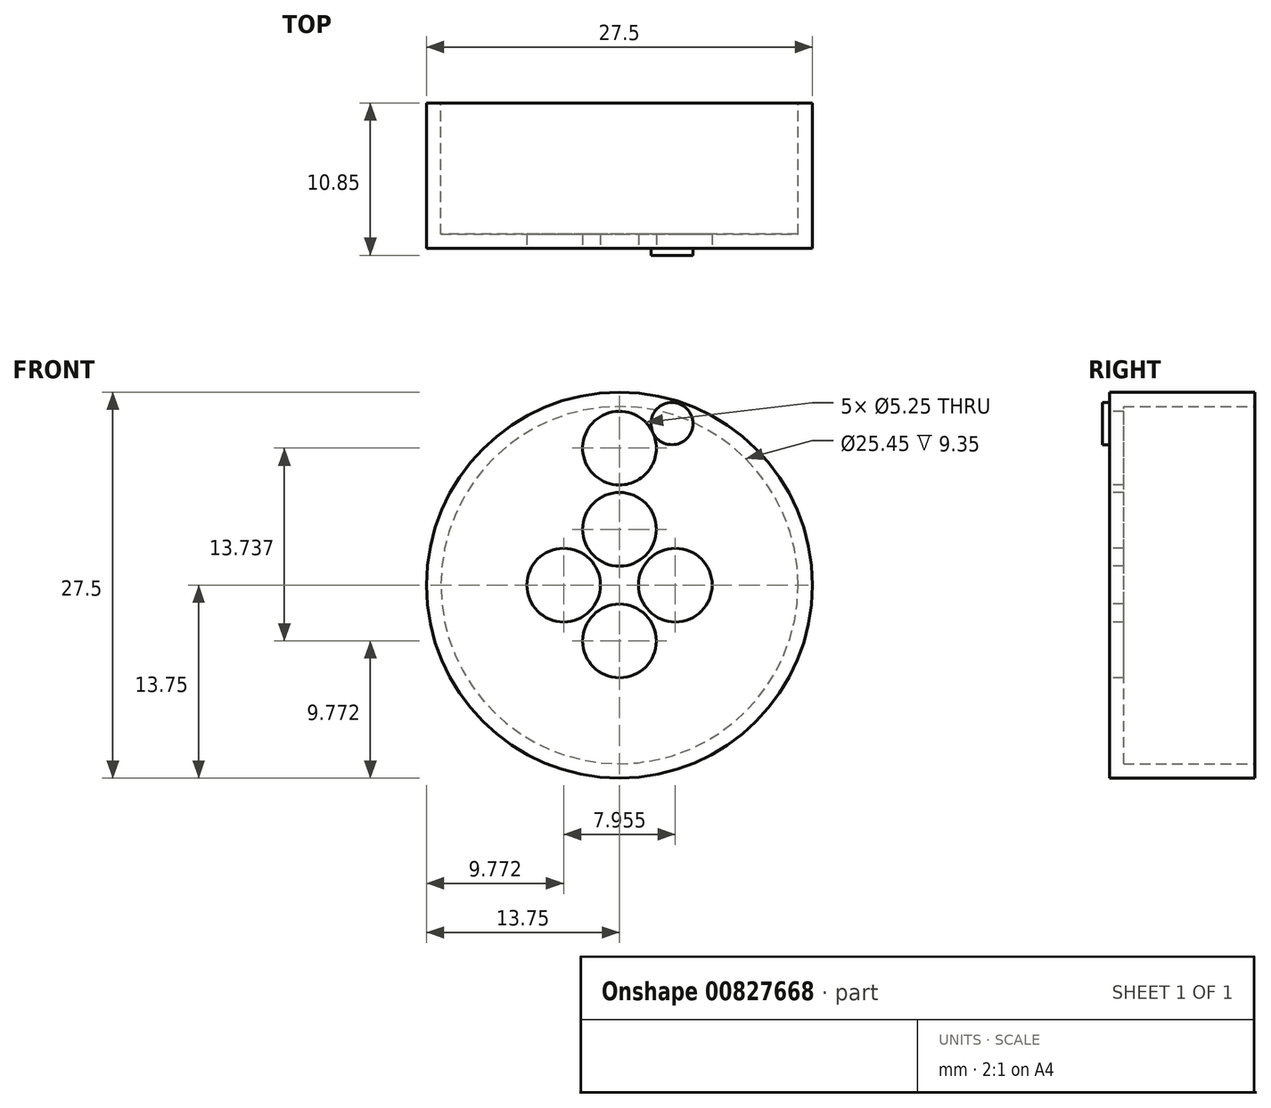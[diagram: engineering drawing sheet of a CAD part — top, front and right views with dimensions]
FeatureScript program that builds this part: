
annotation { "Feature Type Name" : "Feature", "Feature Type Description" : "" }
export const myFeature = defineFeature(function(context is Context, id is Id, definition is map)
    precondition{}
    {
        {
            var Q0;
            Q0=qCreatedBy(makeId("Front.planeOp"),FACE);
            var sketch = newSketch(context, id + "F0", { "sketchPlane" : qUnion([Q0])});
            skCircle(sketch, "E0", {"center": v(0, 0) * mm, "radius": 13.75 * mm});
            skCircle(sketch, "E1", {"center": v(0, 0) * mm, "radius": 12.72 * mm});
            skSolve(sketch);
        }
        {
            var Q0;
            Q0=makeQuery(id+"F0.imprint","IMPRINT",FACE,{"disambiguationData":[TD([[makeQuery(id+"F0.imprint","IMPRINT",EDGE,{"derivedFrom":sQuery(id+"F0.wireOp",EDGE,"E0")}),1.0]])]});
            var Q1;
            Q1=makeQuery(id+"F0.imprint","IMPRINT",FACE,{"disambiguationData":[TD([[makeQuery(id+"F0.imprint","IMPRINT",EDGE,{"derivedFrom":sQuery(id+"F0.wireOp",EDGE,"E1")}),1.0]])]});
            var Q2;
            Q2=sQuery(id+"F0.wireOp",EDGE,"E0");
            extrude(context, id + "F1", {"entities" : qUnion([Q0, Q1]), "surfaceEntities" : qUnion([Q2]), "depth" : 10.35 * mm, "offsetDistance" : 25 * mm});
        }
        {
            var Q0;
            Q0=makeQuery(id+"F0.imprint","IMPRINT",FACE,{"disambiguationData":[TD([[makeQuery(id+"F0.imprint","IMPRINT",EDGE,{"derivedFrom":sQuery(id+"F0.wireOp",EDGE,"E1")}),1.0]])]});
            extrude(context, id + "F2", {"entities" : qUnion([Q0]), "operationType" : NewBodyOperationType.REMOVE, "depth" : 9.35 * mm, "offsetDistance" : 25 * mm});
        }
        {
            var Q0;
            Q0=makeQuery(id+"F1.opExtrude","CAP_FACE",FACE,{"disambiguationData":[OSD([sQuery(id+"F0.wireOp",EDGE,"E0")])],"isStart":false});
            var sketch = newSketch(context, id + "F3", { "sketchPlane" : qUnion([Q0])});
            skCircle(sketch, "E2", {"center": v(0, 9.76) * mm, "radius": 2.62 * mm});
            skCircle(sketch, "E3", {"center": v(0, 0) * mm, "radius": 9.76 * mm, "construction": true});
            skSolve(sketch);
        }
        {
            var Q0;
            Q0 = qSketchRegion(id + "F3", true);
            extrude(context, id + "F4", {"entities" : qUnion([Q0]), "operationType" : NewBodyOperationType.REMOVE, "endBound" : BoundingType.THROUGH_ALL, "oppositeDirection" : true, "depth" : 25 * mm, "offsetDistance" : 25 * mm});
        }
        {
            var Q0;
            Q0=makeQuery(id+"F1.opExtrude","CAP_FACE",FACE,{"disambiguationData":[OSD([sQuery(id+"F0.wireOp",EDGE,"E0")])],"isStart":false});
            var sketch = newSketch(context, id + "F5", { "sketchPlane" : qUnion([Q0])});
            skCircle(sketch, "E4", {"center": v(0, 3.98) * mm, "radius": 2.62 * mm});
            skCircle(sketch, "E5.1.0", {"center": v(3.98, 0) * mm, "radius": 2.62 * mm});
            skCircle(sketch, "E5.2.0", {"center": v(0, -3.98) * mm, "radius": 2.62 * mm});
            skCircle(sketch, "E5.3.0", {"center": v(-3.98, 0) * mm, "radius": 2.62 * mm});
            skPoint(sketch, "E5.center", {"position": v(0, 0) * mm});
            skLineSegment(sketch, "E5.anchor1", {"start": v(0, 0) * mm, "end": v(0, 3.98) * mm, "construction": true});
            skLineSegment(sketch, "E5.anchor2", {"start": v(0, 0) * mm, "end": v(-3.98, 0) * mm, "construction": true});
            skSolve(sketch);
        }
        {
            var Q0;
            Q0=makeQuery(id+"F5.imprint","IMPRINT",FACE,{"disambiguationData":[TD([[makeQuery(id+"F5.imprint","IMPRINT",EDGE,{"derivedFrom":sQuery(id+"F5.wireOp",EDGE,"E4")}),1.0]])]});
            var Q1;
            Q1=makeQuery(id+"F5.imprint","IMPRINT",FACE,{"disambiguationData":[TD([[makeQuery(id+"F5.imprint","IMPRINT",EDGE,{"derivedFrom":sQuery(id+"F5.wireOp",EDGE,"E5.3.0")}),1.0]])]});
            var Q2;
            Q2=makeQuery(id+"F5.imprint","IMPRINT",FACE,{"disambiguationData":[TD([[makeQuery(id+"F5.imprint","IMPRINT",EDGE,{"derivedFrom":sQuery(id+"F5.wireOp",EDGE,"E5.2.0")}),1.0]])]});
            var Q3;
            Q3=makeQuery(id+"F5.imprint","IMPRINT",FACE,{"disambiguationData":[TD([[makeQuery(id+"F5.imprint","IMPRINT",EDGE,{"derivedFrom":sQuery(id+"F5.wireOp",EDGE,"E5.1.0")}),1.0]])]});
            var Q4;
            Q4=sQuery(id+"F5.wireOp",EDGE,"E5.3.0");
            var Q5;
            Q5=sQuery(id+"F5.wireOp",EDGE,"E4");
            var Q6;
            Q6=sQuery(id+"F5.wireOp",EDGE,"E5.1.0");
            var Q7;
            Q7=sQuery(id+"F5.wireOp",EDGE,"E5.2.0");
            extrude(context, id + "F6", {"entities" : qUnion([Q0, Q1, Q2, Q3]), "operationType" : NewBodyOperationType.REMOVE, "surfaceEntities" : qUnion([Q4, Q5, Q6, Q7]), "endBound" : BoundingType.THROUGH_ALL, "oppositeDirection" : true, "depth" : 25 * mm, "offsetDistance" : 25 * mm});
        }
        {
            var Q0;
            Q0=makeQuery(id+"F1.opExtrude","CAP_FACE",FACE,{"disambiguationData":[OSD([sQuery(id+"F0.wireOp",EDGE,"E0")])],"isStart":false});
            var sketch = newSketch(context, id + "F7", { "sketchPlane" : qUnion([Q0])});
            skCircle(sketch, "E6", {"center": v(3.74, 11.5) * mm, "radius": 1.5 * mm});
            skCircle(sketch, "E7", {"center": v(0, 0) * mm, "radius": 12.1 * mm, "construction": true});
            skSolve(sketch);
        }
        {
            var Q0;
            {var subQ0=sQuery(id+"F7.wireOp",EDGE,"E6");var subQ1=sQuery(id+"F3.wireOp",EDGE,"E2");var subQ2=makeQuery(id+"F7.imprint","INTERSECT",VERTEX,{"derivedFrom":[makeQuery(id+"F4.boolean.opBoolean","COPY",EDGE,{"derivedFrom":makeQuery(id+"F4.opExtrude","CAP_EDGE",EDGE,{"disambiguationData":[OSD([subQ1])],"isStart":true})}),subQ0]});Q0=makeQuery(id+"F7.imprint","IMPRINT",FACE,{"disambiguationData":[TD([[makeQuery(id+"F7.imprint","IMPRINT",EDGE,{"disambiguationData":[TD([[subQ2,-1.0]])],"derivedFrom":subQ0}),1.0]])]});}
            var Q1;
            Q1=sQuery(id+"F7.wireOp",EDGE,"E6");
            extrude(context, id + "F8", {"entities" : qUnion([Q0]), "surfaceEntities" : qUnion([Q1]), "depth" : 0.5 * mm, "offsetDistance" : 25 * mm});
        }
    });
